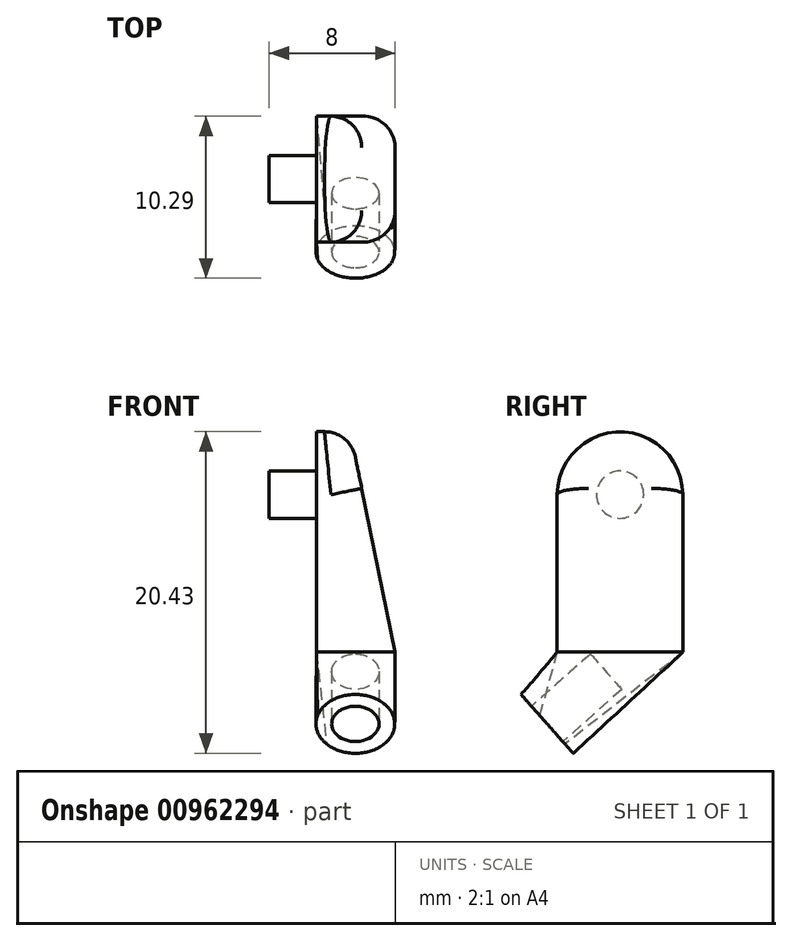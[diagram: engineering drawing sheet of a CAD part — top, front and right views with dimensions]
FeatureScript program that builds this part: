
annotation { "Feature Type Name" : "Feature", "Feature Type Description" : "" }
export const myFeature = defineFeature(function(context is Context, id is Id, definition is map)
    precondition{}
    {
        {
            var Q0;
            Q0=qCreatedBy(makeId("Right.planeOp"),FACE);
            var sketch = newSketch(context, id + "F0", { "sketchPlane" : qUnion([Q0])});
            skCircle(sketch, "E0", {"center": v(0, 0) * mm, "radius": 1.5 * mm});
            skSolve(sketch);
        }
        {
            var Q0;
            Q0 = qSketchRegion(id + "F0", true);
            extrude(context, id + "F1", {"entities" : qUnion([Q0]), "depth" : 3 * mm, "offsetDistance" : 25 * mm});
        }
        {
            var Q0;
            Q0=makeQuery(id+"F1.opExtrude","CAP_FACE",FACE,{"disambiguationData":[OSD([sQuery(id+"F0.wireOp",EDGE,"E0")])],"isStart":false});
            var sketch = newSketch(context, id + "F2", { "sketchPlane" : qUnion([Q0])});
            skArc(sketch, "E1", {"start": v(4, 0) * mm, "mid": v(0, 4) * mm, "end": v(-4, 0) * mm});
            skLineSegment(sketch, "E2.top", {"start": v(4, -10) * mm, "end": v(-4, -10) * mm});
            skLineSegment(sketch, "E2.left", {"start": v(4, 0) * mm, "end": v(4, -10) * mm});
            skLineSegment(sketch, "E2.right", {"start": v(-4, 0) * mm, "end": v(-4, -10) * mm});
            skPoint(sketch, "E2.middle", {"position": v(0, -5) * mm});
            skLineSegment(sketch, "E3", {"start": v(4, -10) * mm, "end": v(-3.1, -16.3) * mm, "construction": true});
            skLineSegment(sketch, "E4", {"start": v(-3.1, -16.3) * mm, "end": v(-6.62, -12.32) * mm, "construction": true});
            skLineSegment(sketch, "E5", {"start": v(-6.62, -12.32) * mm, "end": v(-4, -10) * mm, "construction": true});
            skLineSegment(sketch, "E6", {"start": v(-4.86, -14.3) * mm, "end": v(-2.9, -12.57) * mm});
            skSolve(sketch);
        }
        {
            var Q0;
            Q0 = qSketchRegion(id + "F2", true);
            extrude(context, id + "F3", {"entities" : qUnion([Q0]), "operationType" : NewBodyOperationType.ADD, "depth" : 5 * mm, "offsetDistance" : 25 * mm});
        }
        {
            var Q0;
            Q0=makeQuery(id+"F3.opExtrude","SWEPT_FACE",FACE,{"disambiguationData":[OSD([sQuery(id+"F2.wireOp",EDGE,"E2.right")])]});
            var sketch = newSketch(context, id + "F4", { "sketchPlane" : qUnion([Q0])});
            skLineSegment(sketch, "E7", {"start": v(8, -10) * mm, "end": v(4.26, 8.33) * mm});
            skLineSegment(sketch, "E8", {"start": v(4.26, 8.33) * mm, "end": v(10.7, 8.33) * mm});
            skLineSegment(sketch, "E9", {"start": v(10.7, 8.33) * mm, "end": v(8, -10) * mm});
            skSolve(sketch);
        }
        {
            var Q0;
            Q0 = qSketchRegion(id + "F4", true);
            extrude(context, id + "F5", {"entities" : qUnion([Q0]), "operationType" : NewBodyOperationType.REMOVE, "oppositeDirection" : true, "depth" : 25 * mm, "offsetDistance" : 25 * mm});
        }
        {
            var Q0;
            Q0=makeQuery(id+"F5.boolean.opBoolean","INTERSECT",EDGE,{"derivedFrom":[makeQuery(id+"F3.opExtrude","SWEPT_FACE",FACE,{"disambiguationData":[OSD([sQuery(id+"F2.wireOp",EDGE,"E1")])]}),makeQuery(id+"F5.opExtrude","SWEPT_FACE",FACE,{"disambiguationData":[OSD([sQuery(id+"F4.wireOp",EDGE,"E7")])]})]});
            var Q1;
            Q1=makeQuery(id+"F5.boolean.opBoolean","COPY",EDGE,{"derivedFrom":makeQuery(id+"F5.opExtrude","CAP_EDGE",EDGE,{"disambiguationData":[OSD([sQuery(id+"F4.wireOp",EDGE,"E7")])],"isStart":true})});
            fillet(context, id + "F6", {"entities" : qUnion([Q0, Q1]), "radius" : 2 * mm, "tangentPropagation" : true, "allowEdgeOverflow" : false});
        }
        {
            var Q0;
            Q0=sQuery(id+"F2.wireOp",VERTEX,"E4.end");
            var Q1;
            Q1=sQuery(id+"F2.wireOp",EDGE,"E5");
            cPlane(context, id + "F7", {"entities" : qUnion([Q0, Q1]), "cplaneType" : CPlaneType.LINE_POINT, "offset" : 25 * mm, "width" : 150 * mm, "height" : 150 * mm});
        }
        {
            var Q0;
            Q0=qCreatedBy(id+"F7.planeOp",FACE);
            var sketch = newSketch(context, id + "F8", { "sketchPlane" : qUnion([Q0])});
            skLineSegment(sketch, "E10", {"start": v(-3, -7.48) * mm, "end": v(-9.55, -8.37) * mm, "construction": true});
            skCircle(sketch, "E11", {"center": v(-5.48, -7.82) * mm, "radius": 2.5 * mm});
            skSolve(sketch);
        }
        {
            var Q1;
            Q1=makeQuery(id+"F3.opExtrude","SWEPT_FACE",FACE,{"disambiguationData":[OSD([sQuery(id+"F2.wireOp",EDGE,"E2.top")])]});
            var Q2;
            Q2=makeQuery(id+"F8.imprint","IMPRINT",FACE,{"disambiguationData":[TD([[makeQuery(id+"F8.imprint","IMPRINT",EDGE,{"derivedFrom":sQuery(id+"F8.wireOp",EDGE,"E11")}),1.0]])]});
            loft(context, id + "F9", {"operationType" : NewBodyOperationType.ADD, "sheetProfilesArray" : [{ "sheetProfileEntities" : qUnion([Q1]) }, { "sheetProfileEntities" : qUnion([Q2]) }]});
        }
        {
            var Q0;
            Q0=makeQuery(id+"F8.imprint","IMPRINT",FACE,{"disambiguationData":[TD([[makeQuery(id+"F8.imprint","IMPRINT",EDGE,{"derivedFrom":sQuery(id+"F8.wireOp",EDGE,"E11")}),1.0]])]});
            var sketch = newSketch(context, id + "F10", { "sketchPlane" : qUnion([Q0])});
            skCircle(sketch, "E12", {"center": v(-5.48, -7.82) * mm, "radius": 1.5 * mm});
            skSolve(sketch);
        }
        {
            var Q0;
            Q0 = qSketchRegion(id + "F10", true);
            extrude(context, id + "F11", {"entities" : qUnion([Q0]), "operationType" : NewBodyOperationType.REMOVE, "depth" : 5 * mm, "offsetDistance" : 25 * mm});
        }
        {
            var Q0;
            Q0=makeQuery(id+"F1.opExtrude","SWEPT_BODY",BODY,{"disambiguationData":[OSD([sQuery(id+"F0.wireOp",EDGE,"E0")])]});
            var Q1;
            Q1=makeQuery(id+"F1.opExtrude","CAP_FACE",FACE,{"disambiguationData":[OSD([sQuery(id+"F0.wireOp",EDGE,"E0")])],"isStart":true});
            mirror(context, id + "F12", {"entities" : qUnion([Q0]), "mirrorPlane" : qUnion([Q1])});
        }
        {
            var Q0;
            Q0=makeQuery(id+"F12.opPattern","COPY",BODY,{"derivedFrom":makeQuery(id+"F1.opExtrude","SWEPT_BODY",BODY,{"disambiguationData":[OSD([sQuery(id+"F0.wireOp",EDGE,"E0")])]}),"instanceName":"1"});
            deleteBodies(context, id + "F13", {"entities" : qUnion([Q0])});
        }
    });
